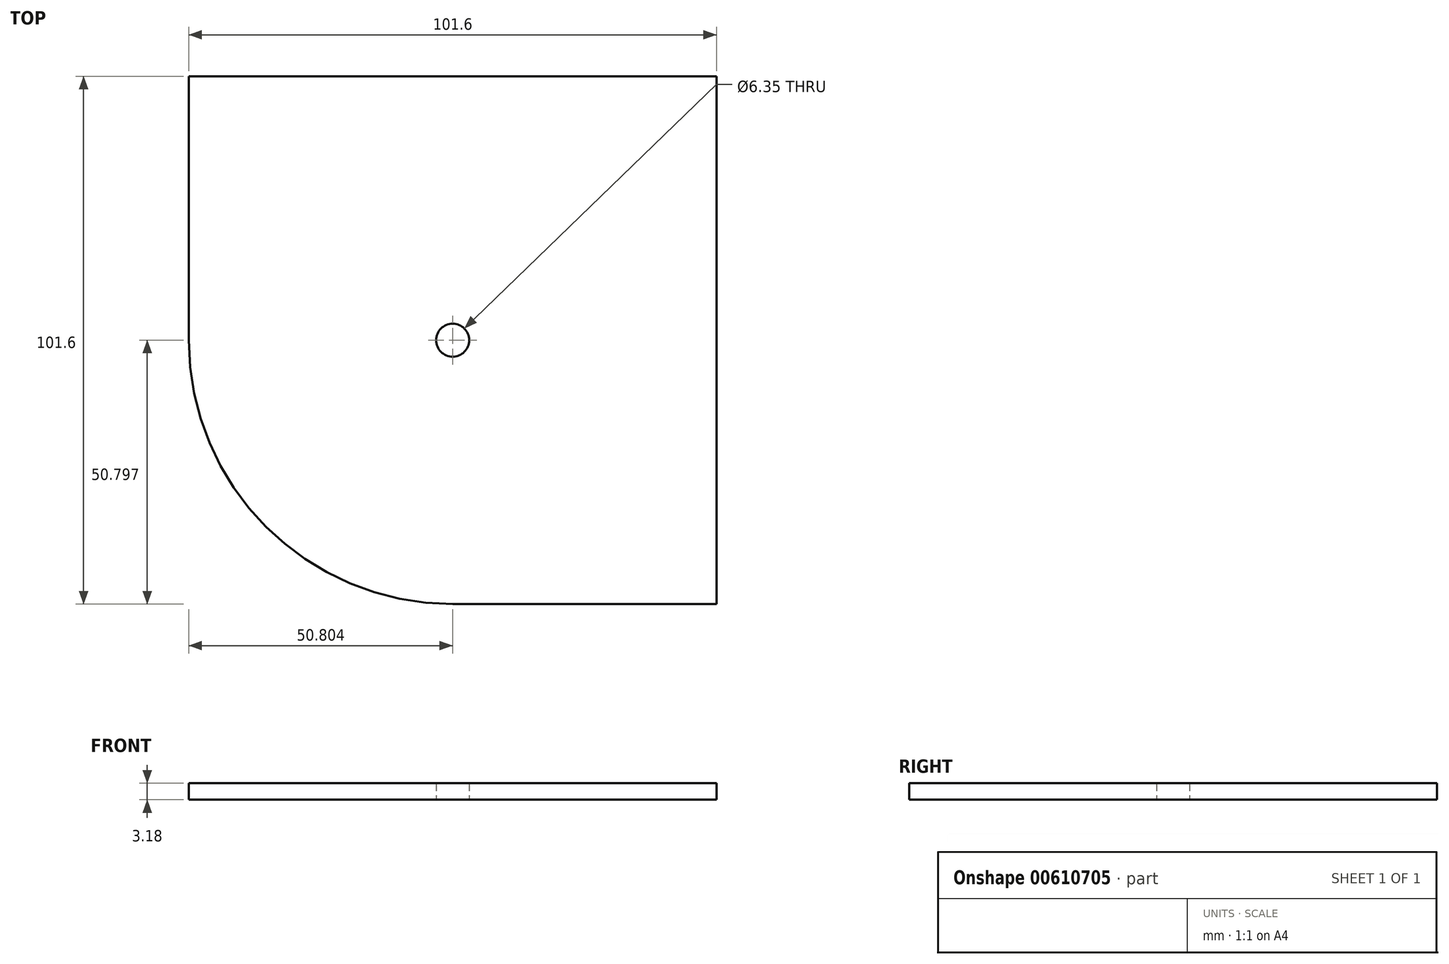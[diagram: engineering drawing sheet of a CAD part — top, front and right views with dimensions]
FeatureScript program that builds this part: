
annotation { "Feature Type Name" : "Feature", "Feature Type Description" : "" }
export const myFeature = defineFeature(function(context is Context, id is Id, definition is map)
    precondition{}
    {
        {
            var Q0;
            Q0=qCreatedBy(makeId("Top.planeOp"),FACE);
            var sketch = newSketch(context, id + "F0", { "sketchPlane" : qUnion([Q0])});
            skLineSegment(sketch, "E0.bottom", {"start": v(24.88, -20) * mm, "end": v(75.68, -20) * mm});
            skLineSegment(sketch, "E0.top", {"start": v(-25.92, 81.6) * mm, "end": v(75.68, 81.6) * mm});
            skLineSegment(sketch, "E0.left", {"start": v(-25.92, 30.8) * mm, "end": v(-25.92, 81.6) * mm});
            skLineSegment(sketch, "E0.right", {"start": v(75.68, -20) * mm, "end": v(75.68, 81.6) * mm});
            skLineSegment(sketch, "E1", {"start": v(-25.92, 81.6) * mm, "end": v(75.68, -20) * mm});
            skCircle(sketch, "E2", {"center": v(24.88, 30.8) * mm, "radius": 50.8 * mm});
            skCircle(sketch, "E3", {"center": v(24.88, 30.8) * mm, "radius": 3.18 * mm});
            skSolve(sketch);
        }
        {
            var Q0;
            {var subQ0=sQuery(id+"F0.wireOp",EDGE,"E0.left");Q0=makeQuery(id+"F0.imprint","IMPRINT",FACE,{"disambiguationData":[TD([[makeQuery(id+"F0.imprint","IMPRINT",EDGE,{"derivedFrom":subQ0}),-1.0]])]});}
            var Q1;
            {var subQ0=sQuery(id+"F0.wireOp",EDGE,"E2");var subQ2=sQuery(id+"F0.wireOp",EDGE,"E1");var subQ3=makeQuery(id+"F0.imprint","INTERSECT",VERTEX,{"disambiguationData":[OD(0.0)],"derivedFrom":[subQ2,subQ0]});Q1=makeQuery(id+"F0.imprint","IMPRINT",FACE,{"disambiguationData":[TD([[makeQuery(id+"F0.imprint","IMPRINT",EDGE,{"disambiguationData":[TD([[subQ3,-1.0]])],"derivedFrom":subQ2}),-1.0]])]});}
            var Q2;
            {var subQ0=sQuery(id+"F0.wireOp",EDGE,"E0.bottom");Q2=makeQuery(id+"F0.imprint","IMPRINT",FACE,{"disambiguationData":[TD([[makeQuery(id+"F0.imprint","IMPRINT",EDGE,{"derivedFrom":subQ0}),1.0]])]});}
            var Q3;
            {var subQ1=sQuery(id+"F0.wireOp",EDGE,"E0.right");var subQ3=sQuery(id+"F0.wireOp",EDGE,"E2");var subQ4=makeQuery(id+"F0.imprint","INTERSECT",VERTEX,{"derivedFrom":[subQ1,subQ3]});Q3=makeQuery(id+"F0.imprint","IMPRINT",FACE,{"disambiguationData":[TD([[makeQuery(id+"F0.imprint","IMPRINT",EDGE,{"disambiguationData":[TD([[subQ4,1.0]])],"derivedFrom":subQ3}),-1.0]])]});}
            var Q4;
            {var subQ0=sQuery(id+"F0.wireOp",EDGE,"E2");var subQ4=sQuery(id+"F0.wireOp",EDGE,"E1");var subQ7=makeQuery(id+"F0.imprint","INTERSECT",VERTEX,{"disambiguationData":[OD(0.0)],"derivedFrom":[subQ4,subQ0]});Q4=makeQuery(id+"F0.imprint","IMPRINT",FACE,{"disambiguationData":[TD([[makeQuery(id+"F0.imprint","IMPRINT",EDGE,{"disambiguationData":[TD([[subQ7,-1.0]])],"derivedFrom":subQ4}),1.0]])]});}
            var Q5;
            {var subQ1=sQuery(id+"F0.wireOp",EDGE,"E0.top");var subQ3=sQuery(id+"F0.wireOp",EDGE,"E2");var subQ4=makeQuery(id+"F0.imprint","INTERSECT",VERTEX,{"derivedFrom":[subQ1,subQ3]});Q5=makeQuery(id+"F0.imprint","IMPRINT",FACE,{"disambiguationData":[TD([[makeQuery(id+"F0.imprint","IMPRINT",EDGE,{"disambiguationData":[TD([[subQ4,-1.0]])],"derivedFrom":subQ3}),-1.0]])]});}
            var Q6;
            {var subQ0=sQuery(id+"F0.wireOp",EDGE,"E0.right");var subQ1=sQuery(id+"F0.wireOp",EDGE,"E0.top");var subQ2=makeQuery(id+"F0.imprint","INTERSECT",VERTEX,{"derivedFrom":[subQ1,subQ0]});Q6=makeQuery(id+"F0.imprint","IMPRINT",FACE,{"disambiguationData":[TD([[makeQuery(id+"F0.imprint","IMPRINT",EDGE,{"disambiguationData":[TD([[subQ2,1.0]])],"derivedFrom":subQ1}),-1.0]])]});}
            extrude(context, id + "F1", {"entities" : qUnion([Q0, Q1, Q2, Q3, Q4, Q5, Q6]), "depth" : 3.17 * mm, "offsetDistance" : 25.4 * mm});
        }
    });
